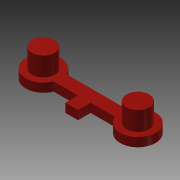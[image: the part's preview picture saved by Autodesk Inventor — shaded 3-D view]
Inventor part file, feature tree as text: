
AUTODESK INVENTOR PART (.ipt)
format: ipt  version: 2014 (Build 180170000, 170)  size: 99,840 bytes
history: native  units: mm
features: extrude x2, sketch x2, other x1
ambient origin geometry x8: Origin, YZ Plane, XZ Plane, XY Plane, X Axis, Y Axis, Z Axis, Center Point
bodies: Body1 (feature_tree)
feature tree (5):
  other  "Твердое тело1"
  extrude  "Выдавливание1"  Depth=5.6mm
  extrude  "Выдавливание2"  Depth=5.6mm
  sketch  "Эскиз1"
  sketch  "Эскиз2"
